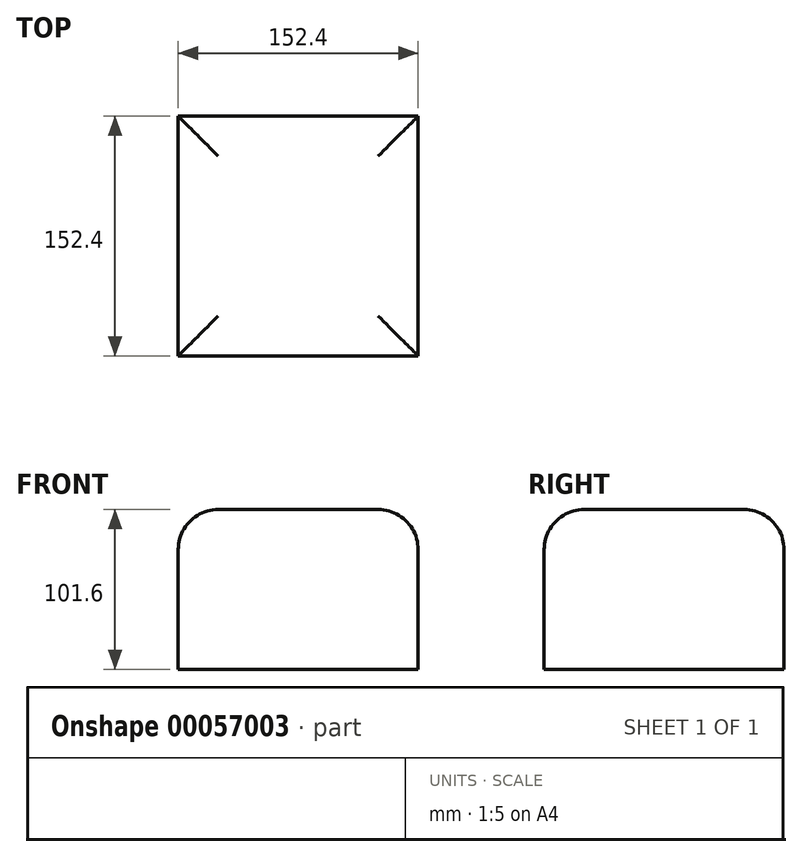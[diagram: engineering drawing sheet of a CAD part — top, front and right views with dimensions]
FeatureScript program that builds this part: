
annotation { "Feature Type Name" : "Feature", "Feature Type Description" : "" }
export const myFeature = defineFeature(function(context is Context, id is Id, definition is map)
    precondition{}
    {
        {
            var Q0;
            Q0=qCreatedBy(makeId("Front.planeOp"),FACE);
            var sketch = newSketch(context, id + "F0", { "sketchPlane" : qUnion([Q0])});
            skLineSegment(sketch, "E0.bottom", {"start": v(-76.2, 50.8) * mm, "end": v(76.2, 50.8) * mm});
            skLineSegment(sketch, "E0.top", {"start": v(-76.2, -50.8) * mm, "end": v(76.2, -50.8) * mm});
            skLineSegment(sketch, "E0.left", {"start": v(-76.2, 50.8) * mm, "end": v(-76.2, -50.8) * mm});
            skLineSegment(sketch, "E0.right", {"start": v(76.2, 50.8) * mm, "end": v(76.2, -50.8) * mm});
            skSolve(sketch);
        }
        {
            var Q0;
            Q0=makeQuery(id+"F0.imprint","IMPRINT",FACE,{"disambiguationData":[TD([[makeQuery(id+"F0.imprint","IMPRINT",EDGE,{"derivedFrom":sQuery(id+"F0.wireOp",EDGE,"E0.bottom")}),-1.0]])]});
            extrude(context, id + "F1", {"entities" : qUnion([Q0]), "oppositeDirection" : true, "depth" : 152.4 * mm});
        }
        {
            var Q0;
            Q0=makeQuery(id+"F1.opExtrude","SWEPT_EDGE",EDGE,{"disambiguationData":[OSD([sQuery(id+"F0.wireOp",EDGE,"E0.bottom"),sQuery(id+"F0.wireOp",EDGE,"E0.left")])]});
            var Q1;
            Q1=makeQuery(id+"F1.opExtrude","CAP_EDGE",EDGE,{"disambiguationData":[OSD([sQuery(id+"F0.wireOp",EDGE,"E0.bottom")])],"isStart":false});
            var Q2;
            Q2=makeQuery(id+"F1.opExtrude","SWEPT_EDGE",EDGE,{"disambiguationData":[OSD([sQuery(id+"F0.wireOp",EDGE,"E0.bottom"),sQuery(id+"F0.wireOp",EDGE,"E0.right")])]});
            var Q3;
            Q3=makeQuery(id+"F1.opExtrude","CAP_EDGE",EDGE,{"disambiguationData":[OSD([sQuery(id+"F0.wireOp",EDGE,"E0.bottom")])],"isStart":true});
            fillet(context, id + "F2", {"entities" : qUnion([Q0, Q1, Q2, Q3]), "radius" : 25.4 * mm, "tangentPropagation" : true, "allowEdgeOverflow" : false});
        }
    });
